# Revit family: Acoustical Suspension System - USG - TRUE™ WOOD - 2D
name_source: partatom
category: Detail Items
revit_build: Autodesk Revit 2015 (Build: 20140606_1530(x64)
units: mm (PartAtom-declared; Revit-internal decimal feet)

## types (3) — shared parameters
Assembly Code = C3030200
Color = Wood Tone
Manufacturer = USG
Material = Wood Veneer Panels
Product Documentation Link = https://www.usg.com
Thickness = 3/4"
Type Comments = 3/4" Wood Veneer
URL = www.usg.com
USG Literature = IC558

## per-type parameters (varying)
| type | Description | Grid Options | Model | Profile Offset | Tee Offset | WDAR | WDFL, WDSL |
| WDFL - 3/4" | TRUE™ WOOD with Fineline Edge | USG Centricitee DXT, USG Fineline DXF, USG Fineline 1/8 DXFF, USG DXI | WDFL | 3/16" | 13/32" | No | Yes |
| WDSL - 3/4" | TRUE™ WOOD with Shadowline Edge | USG DX/DXL | WDSL | 13/32" | 13/32" | No | Yes |
| WDAR - 3/4" | TRUE™ WOOD with Accessible Reveal Edge | USG DX/DXL | WDAR | 3/32" | 1/2" | Yes | No |

## geometry (parser evidence)
native form markers: Sweep x1
no freeform markers — native parametric forms only
